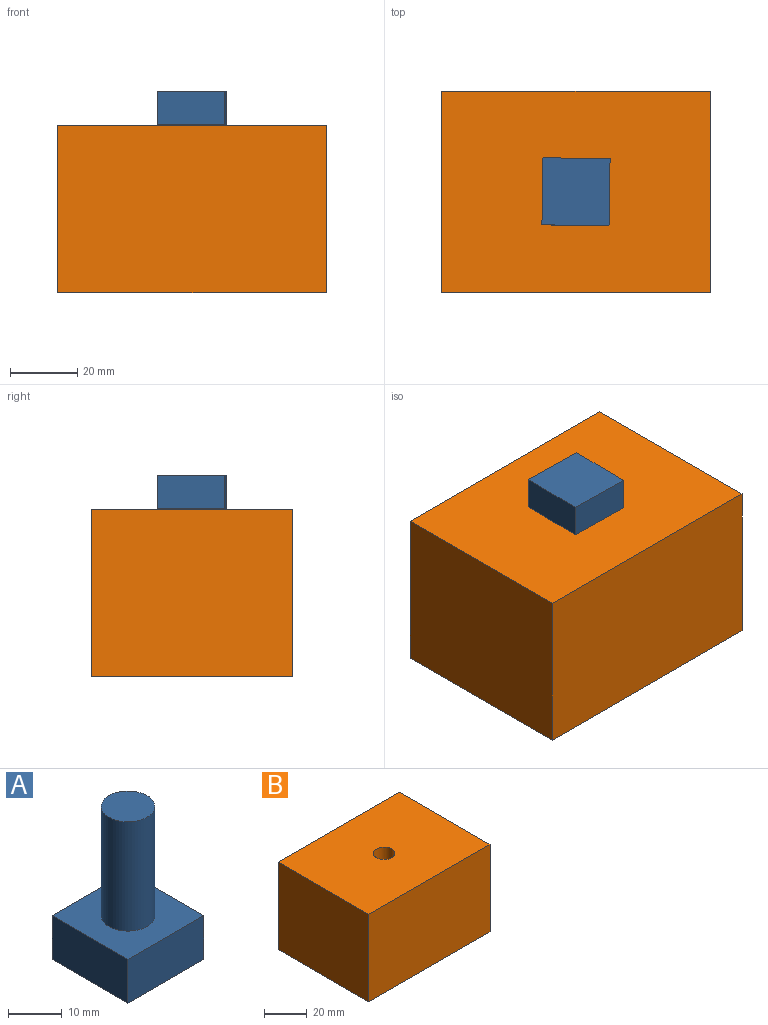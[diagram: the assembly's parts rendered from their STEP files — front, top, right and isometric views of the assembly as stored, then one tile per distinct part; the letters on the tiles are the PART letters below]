
ASSEMBLY  parts=2 mates=1
PART A: 8 faces, bbox 20x20x35 mm
  f0: plane 20x10mm, normal (1,0,0), area 200mm2, adj f1,f3,f4,f5
  f1: plane 20x10mm, normal (0,1,0), area 200mm2, adj f0,f2,f4,f5
  f2: plane 20x10mm, normal (-1,0,0), area 200mm2, adj f1,f3,f4,f5
  f3: plane 20x10mm, normal (0,-1,0), area 200mm2, adj f0,f2,f4,f5
  f4: plane 20x20mm, normal (0,0,1), area 321.5mm2, adj f0,f1,f2,f3,f6
  f5: plane 20x20mm, normal (0,0,-1), area 400mm2, adj f0,f1,f2,f3
  f6: cylinder r=5mm len=25mm, axis (0,0,-1), area 785.4mm2, adj f4,f7
  f7: plane 10x10mm, normal (0,0,1), area 78.5mm2, adj f6
PART B: 8 faces, bbox 80x60x50 mm
  f0: plane 80x50mm, normal (0,-1,0), area 4000mm2, adj f1,f3,f4,f5
  f1: plane 60x50mm, normal (1,0,0), area 3000mm2, adj f0,f2,f4,f5
  f2: plane 80x50mm, normal (0,1,0), area 4000mm2, adj f1,f3,f4,f5
  f3: plane 60x50mm, normal (-1,0,0), area 3000mm2, adj f0,f2,f4,f5
  f4: plane 80x60mm, normal (0,0,1), area 4721.5mm2, adj f0,f1,f2,f3,f6
  f5: plane 80x60mm, normal (0,0,-1), area 4800mm2, adj f0,f1,f2,f3
  f6: cylinder r=5mm len=25mm, axis (0,0,1), area 785.4mm2, adj f4,f7
  f7: plane 10x10mm, normal (0,0,1), area 78.5mm2, adj f6
PLACE A rot(axis=(-0.01,-1,0),180deg) t=(-1.9,5.43,44.85)mm
PLACE B t=(-1.9,5.43,-15.22)mm fixed
MATE cylindrical B.f6 <-> A.f6  axis (0,0,1) through (-1.9,5.43,34.78)mm
